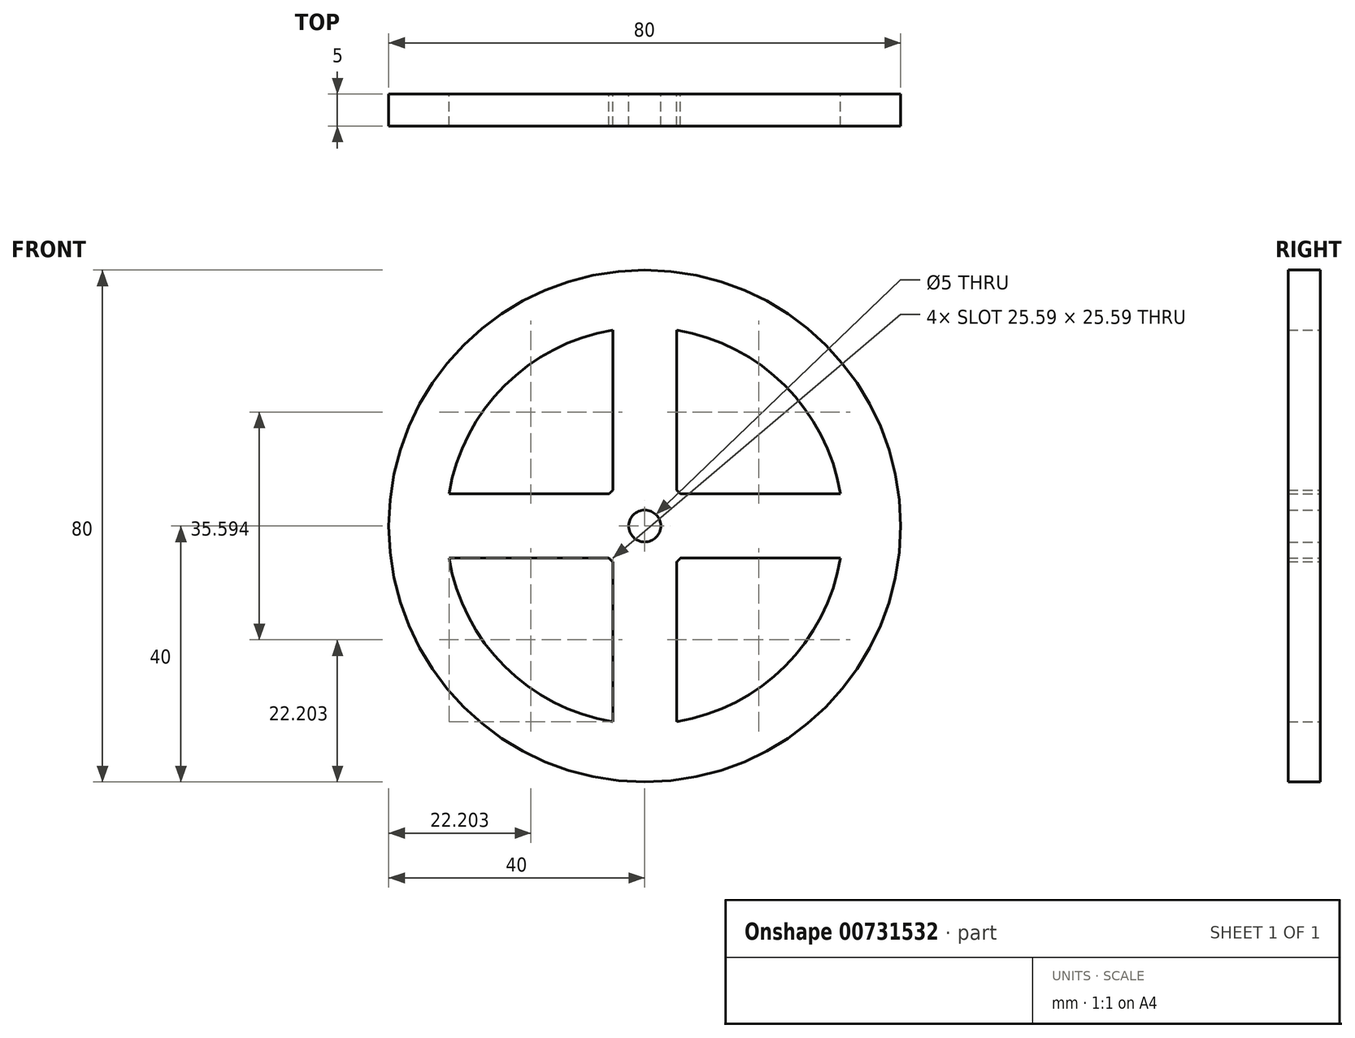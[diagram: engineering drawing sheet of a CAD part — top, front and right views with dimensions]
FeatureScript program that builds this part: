
annotation { "Feature Type Name" : "Feature", "Feature Type Description" : "" }
export const myFeature = defineFeature(function(context is Context, id is Id, definition is map)
    precondition{}
    {
        {
            var Q0;
            Q0=qCreatedBy(makeId("Front.planeOp"),FACE);
            var sketch = newSketch(context, id + "F0", { "sketchPlane" : qUnion([Q0])});
            skCircle(sketch, "E0", {"center": v(0, 0) * mm, "radius": 40 * mm});
            skArc(sketch, "E1", {"start": v(-5, 30.6) * mm, "mid": v(-21.92, 21.92) * mm, "end": v(-30.6, 5) * mm});
            skArc(sketch, "E2", {"start": v(-5, 5.6) * mm, "mid": v(-5.3, 5.3) * mm, "end": v(-5.6, 5) * mm});
            skCircle(sketch, "E3", {"center": v(0, 0) * mm, "radius": 2.5 * mm});
            skLineSegment(sketch, "E4", {"start": v(0, 0) * mm, "end": v(0, 31) * mm, "construction": true});
            skLineSegment(sketch, "E5", {"start": v(0, 0) * mm, "end": v(-31, 0) * mm, "construction": true});
            skLineSegment(sketch, "E6", {"start": v(0, 0) * mm, "end": v(0, -31) * mm, "construction": true});
            skLineSegment(sketch, "E7", {"start": v(0, 0) * mm, "end": v(31, 0) * mm, "construction": true});
            skLineSegment(sketch, "E8.0", {"start": v(5, 5.6) * mm, "end": v(5, 30.6) * mm});
            skLineSegment(sketch, "E9.0", {"start": v(-5, 5.6) * mm, "end": v(-5, 30.6) * mm});
            skLineSegment(sketch, "E10.0", {"start": v(-5.6, 5) * mm, "end": v(-30.6, 5) * mm});
            skLineSegment(sketch, "E11.0", {"start": v(-5.6, -5) * mm, "end": v(-30.6, -5) * mm});
            skLineSegment(sketch, "E12.0", {"start": v(-5, -5.6) * mm, "end": v(-5, -30.6) * mm});
            skLineSegment(sketch, "E13.0", {"start": v(5, -5.6) * mm, "end": v(5, -30.6) * mm});
            skLineSegment(sketch, "E14.0", {"start": v(5.6, -5) * mm, "end": v(30.6, -5) * mm});
            skLineSegment(sketch, "E15.0", {"start": v(5.6, 5) * mm, "end": v(30.6, 5) * mm});
            skArc(sketch, "E16.trimOffspring", {"start": v(-5.6, -5) * mm, "mid": v(-5.3, -5.3) * mm, "end": v(-5, -5.6) * mm});
            skArc(sketch, "E17.trimOffspring", {"start": v(5, -5.6) * mm, "mid": v(5.3, -5.3) * mm, "end": v(5.6, -5) * mm});
            skArc(sketch, "E18.trimOffspring", {"start": v(5.6, 5) * mm, "mid": v(5.3, 5.3) * mm, "end": v(5, 5.6) * mm});
            skArc(sketch, "E19.trimOffspring", {"start": v(30.6, 5) * mm, "mid": v(21.92, 21.92) * mm, "end": v(5, 30.6) * mm});
            skArc(sketch, "E20.trimOffspring", {"start": v(-30.6, -5) * mm, "mid": v(-21.92, -21.92) * mm, "end": v(-5, -30.6) * mm});
            skArc(sketch, "E21.trimOffspring", {"start": v(5, -30.6) * mm, "mid": v(21.92, -21.92) * mm, "end": v(30.6, -5) * mm});
            skSolve(sketch);
        }
        {
            var Q0;
            Q0=makeQuery(id+"F0.imprint","IMPRINT",FACE,{"disambiguationData":[TD([[makeQuery(id+"F0.imprint","IMPRINT",EDGE,{"derivedFrom":sQuery(id+"F0.wireOp",EDGE,"E0")}),1.0]])]});
            extrude(context, id + "F1", {"entities" : qUnion([Q0]), "endBound" : BoundingType.SYMMETRIC, "depth" : 5 * mm, "offsetDistance" : 25 * mm});
        }
    });
